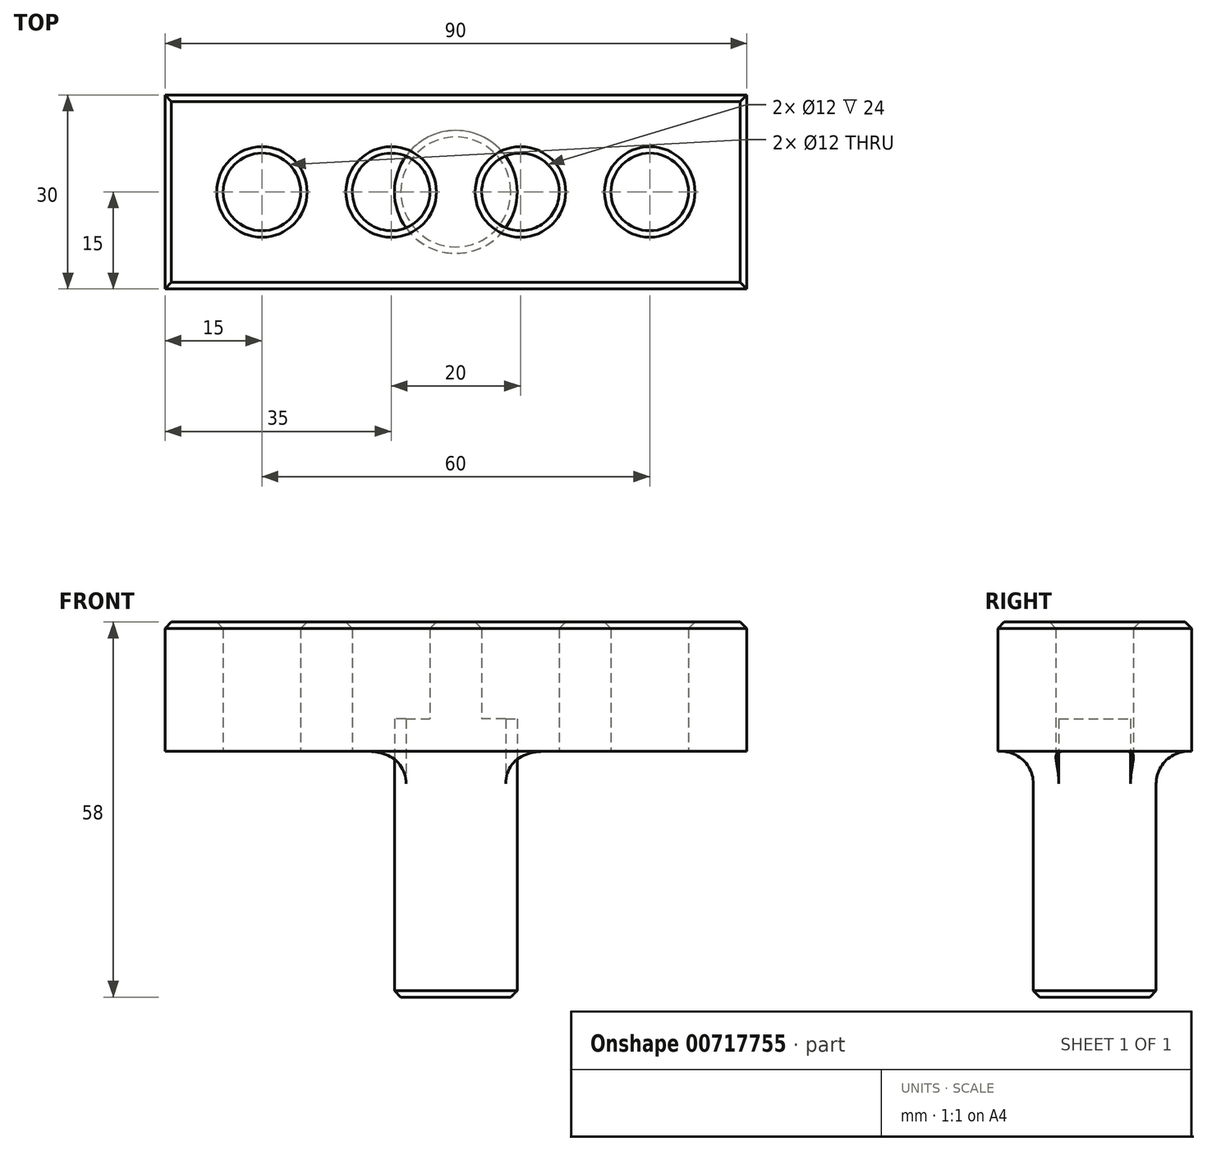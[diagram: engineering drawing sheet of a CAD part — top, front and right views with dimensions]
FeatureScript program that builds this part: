
annotation { "Feature Type Name" : "Feature", "Feature Type Description" : "" }
export const myFeature = defineFeature(function(context is Context, id is Id, definition is map)
    precondition{}
    {
        {
            var Q0;
            Q0=qCreatedBy(makeId("Top.planeOp"),FACE);
            var sketch = newSketch(context, id + "F0", { "sketchPlane" : qUnion([Q0])});
            skLineSegment(sketch, "E0.bottom", {"start": v(-45, 15) * mm, "end": v(45, 15) * mm});
            skLineSegment(sketch, "E0.top", {"start": v(-45, -15) * mm, "end": v(45, -15) * mm});
            skLineSegment(sketch, "E0.left", {"start": v(-45, 15) * mm, "end": v(-45, -15) * mm});
            skLineSegment(sketch, "E0.right", {"start": v(45, 15) * mm, "end": v(45, -15) * mm});
            skPoint(sketch, "E0.middle", {"position": v(0, 0) * mm});
            skLineSegment(sketch, "E1", {"start": v(-45, -15) * mm, "end": v(-45, 0) * mm, "construction": true});
            skLineSegment(sketch, "E2", {"start": v(-45, 0) * mm, "end": v(45, 0) * mm, "construction": true});
            skLineSegment(sketch, "E3", {"start": v(45, 0) * mm, "end": v(45, 10) * mm, "construction": true});
            skLineSegment(sketch, "E4", {"start": v(45, 10) * mm, "end": v(-127.47, 10) * mm, "construction": true});
            skLineSegment(sketch, "E5", {"start": v(-45, 0) * mm, "end": v(-30, 0) * mm, "construction": true});
            skLineSegment(sketch, "E6", {"start": v(-30, 0) * mm, "end": v(-30, -10) * mm, "construction": true});
            skCircle(sketch, "E7", {"center": v(-30, 0) * mm, "radius": 6 * mm});
            skCircle(sketch, "E8.1.0.0", {"center": v(-10, 0) * mm, "radius": 6 * mm});
            skCircle(sketch, "E8.2.0.0", {"center": v(10, 0) * mm, "radius": 6 * mm});
            skCircle(sketch, "E8.3.0.0", {"center": v(30, 0) * mm, "radius": 6 * mm});
            skLineSegment(sketch, "E8.direction1", {"start": v(-30, 0) * mm, "end": v(-10, 0) * mm, "construction": true});
            skSolve(sketch);
        }
        {
            var Q0;
            Q0=makeQuery(id+"F0.imprint","IMPRINT",FACE,{"disambiguationData":[TD([[makeQuery(id+"F0.imprint","IMPRINT",EDGE,{"derivedFrom":sQuery(id+"F0.wireOp",EDGE,"E0.bottom")}),-1.0]])]});
            extrude(context, id + "F1", {"entities" : qUnion([Q0]), "depth" : 20 * mm});
        }
        {
            var Q0;
            Q0=makeQuery(id+"F1.opExtrude","CAP_FACE",FACE,{"disambiguationData":[OSD([sQuery(id+"F0.wireOp",EDGE,"E0.bottom"),sQuery(id+"F0.wireOp",EDGE,"E0.top"),sQuery(id+"F0.wireOp",EDGE,"E0.left"),sQuery(id+"F0.wireOp",EDGE,"E0.right"),sQuery(id+"F0.wireOp",EDGE,"E7"),sQuery(id+"F0.wireOp",EDGE,"E8.1.0.0"),sQuery(id+"F0.wireOp",EDGE,"E8.2.0.0"),sQuery(id+"F0.wireOp",EDGE,"E8.3.0.0"),sQuery(id+"F0.wireOp",EDGE,"E8.4.0.0"),sQuery(id+"F0.wireOp",EDGE,"E8.5.0.0"),sQuery(id+"F0.wireOp",EDGE,"E8.6.0.0"),sQuery(id+"F0.wireOp",EDGE,"E8.7.0.0"),sQuery(id+"F0.wireOp",EDGE,"E8.8.0.0"),sQuery(id+"F0.wireOp",EDGE,"E8.9.0.0"),sQuery(id+"F0.wireOp",EDGE,"E8.10.0.0"),sQuery(id+"F0.wireOp",EDGE,"E8.11.0.0")])],"isStart":false});
            chamfer(context, id + "F2", {"entities" : qUnion([Q0]), "width" : 1 * mm, "tangentPropagation" : true});
        }
        {
            var Q0;
            Q0=qCreatedBy(makeId("Top.planeOp"),FACE);
            var sketch = newSketch(context, id + "F3", { "sketchPlane" : qUnion([Q0])});
            skCircle(sketch, "E9", {"center": v(0, 0) * mm, "radius": 9.5 * mm});
            skSolve(sketch);
        }
        {
            var Q0;
            Q0=qSketchRegion(id+"F3",true);
            extrude(context, id + "F4", {"entities" : qUnion([Q0]), "operationType" : NewBodyOperationType.ADD, "depth" : 5 * mm, "hasSecondDirection" : true, "secondDirectionOppositeDirection" : true, "secondDirectionDepth" : 38 * mm});
        }
        {
            var Q0;
            Q0=makeQuery(id+"F4.opExtrude","CAP_EDGE",EDGE,{"disambiguationData":[OSD([sQuery(id+"F3.wireOp",EDGE,"E9")])],"isStart":true});
            chamfer(context, id + "F5", {"entities" : qUnion([Q0]), "width" : 1 * mm, "tangentPropagation" : true});
        }
        {
            var Q0;
            Q0=makeQuery(id+"F4.boolean.opBoolean","INTERSECT",EDGE,{"disambiguationData":[OD(0.0)],"derivedFrom":[makeQuery(id+"F1.opExtrude","CAP_FACE",FACE,{"disambiguationData":[OSD([sQuery(id+"F0.wireOp",EDGE,"E0.bottom"),sQuery(id+"F0.wireOp",EDGE,"E0.top"),sQuery(id+"F0.wireOp",EDGE,"E0.left"),sQuery(id+"F0.wireOp",EDGE,"E0.right"),sQuery(id+"F0.wireOp",EDGE,"E7"),sQuery(id+"F0.wireOp",EDGE,"E8.1.0.0"),sQuery(id+"F0.wireOp",EDGE,"E8.2.0.0"),sQuery(id+"F0.wireOp",EDGE,"E8.3.0.0"),sQuery(id+"F0.wireOp",EDGE,"E8.4.0.0"),sQuery(id+"F0.wireOp",EDGE,"E8.5.0.0"),sQuery(id+"F0.wireOp",EDGE,"E8.6.0.0"),sQuery(id+"F0.wireOp",EDGE,"E8.7.0.0"),sQuery(id+"F0.wireOp",EDGE,"E8.8.0.0"),sQuery(id+"F0.wireOp",EDGE,"E8.9.0.0"),sQuery(id+"F0.wireOp",EDGE,"E8.10.0.0"),sQuery(id+"F0.wireOp",EDGE,"E8.11.0.0")])],"isStart":true}),makeQuery(id+"F4.opExtrude","SWEPT_FACE",FACE,{"disambiguationData":[OSD([sQuery(id+"F3.wireOp",EDGE,"E9")])]})]});
            var Q1;
            Q1=makeQuery(id+"F4.boolean.opBoolean","INTERSECT",EDGE,{"disambiguationData":[OD(1.0)],"derivedFrom":[makeQuery(id+"F1.opExtrude","CAP_FACE",FACE,{"disambiguationData":[OSD([sQuery(id+"F0.wireOp",EDGE,"E0.bottom"),sQuery(id+"F0.wireOp",EDGE,"E0.top"),sQuery(id+"F0.wireOp",EDGE,"E0.left"),sQuery(id+"F0.wireOp",EDGE,"E0.right"),sQuery(id+"F0.wireOp",EDGE,"E7"),sQuery(id+"F0.wireOp",EDGE,"E8.1.0.0"),sQuery(id+"F0.wireOp",EDGE,"E8.2.0.0"),sQuery(id+"F0.wireOp",EDGE,"E8.3.0.0"),sQuery(id+"F0.wireOp",EDGE,"E8.4.0.0"),sQuery(id+"F0.wireOp",EDGE,"E8.5.0.0"),sQuery(id+"F0.wireOp",EDGE,"E8.6.0.0"),sQuery(id+"F0.wireOp",EDGE,"E8.7.0.0"),sQuery(id+"F0.wireOp",EDGE,"E8.8.0.0"),sQuery(id+"F0.wireOp",EDGE,"E8.9.0.0"),sQuery(id+"F0.wireOp",EDGE,"E8.10.0.0"),sQuery(id+"F0.wireOp",EDGE,"E8.11.0.0")])],"isStart":true}),makeQuery(id+"F4.opExtrude","SWEPT_FACE",FACE,{"disambiguationData":[OSD([sQuery(id+"F3.wireOp",EDGE,"E9")])]})]});
            fillet(context, id + "F6", {"entities" : qUnion([Q0, Q1]), "radius" : 5 * mm, "tangentPropagation" : true, "allowEdgeOverflow" : false});
        }
    });
